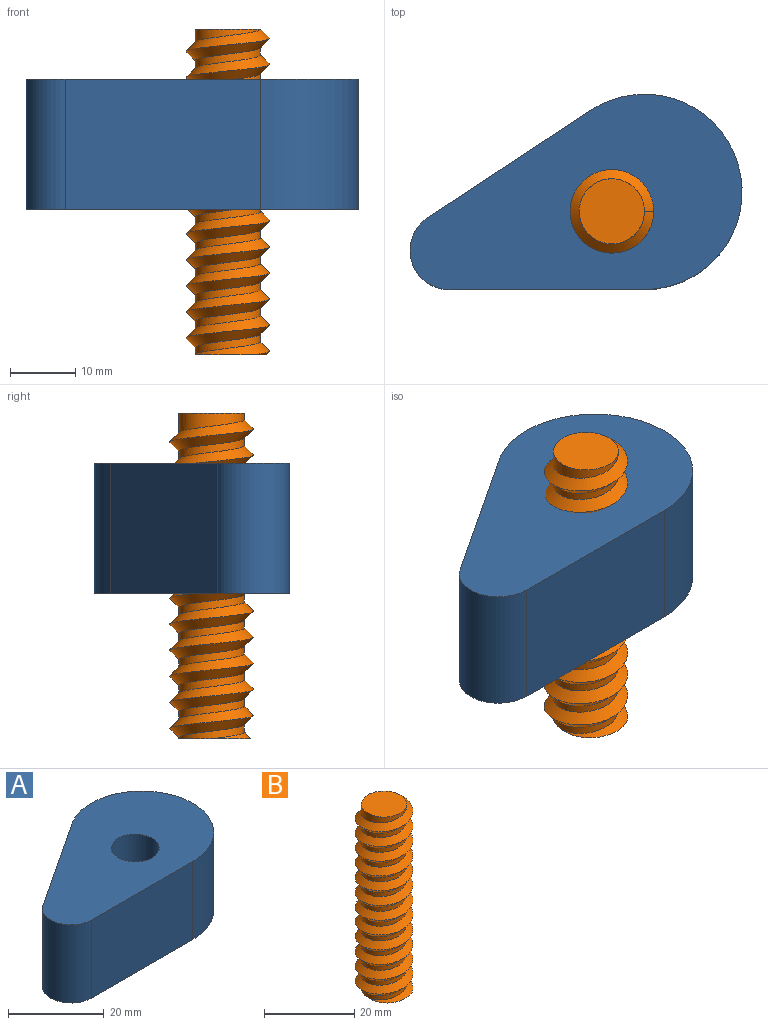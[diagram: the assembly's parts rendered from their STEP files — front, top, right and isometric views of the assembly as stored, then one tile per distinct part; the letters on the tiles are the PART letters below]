
ASSEMBLY  parts=2 mates=1
PART A: 7 faces, bbox 51x30x20 mm
  f0: plane 25.05x20mm, normal (-0.55,0.83,0), area 600mm2, adj f1,f3,f4,f5
  f1: cylinder r=6mm len=20mm, axis (0,0,-1), area 307mm2, adj f0,f2,f4,f5
  f2: plane 30x20mm, normal (0,-1,0), area 600mm2, adj f1,f3,f4,f5
  f3: cylinder r=15mm len=30mm, axis (0,0,-1), area 1117.4mm2, adj f0,f2,f4,f5
  f4: plane 51x30mm, normal (0,0,1), area 1016.5mm2, adj f0,f1,f2,f3,f6
  f5: plane 51x30mm, normal (0,0,-1), area 1016.5mm2, adj f0,f1,f2,f3,f6
  f6: cylinder r=5mm len=20mm, axis (0,0,1), area 628.3mm2, adj f4,f5
PART B: 6 faces, bbox 13.7x15.6x52.3 mm
  f0: cylinder r=5mm len=50mm, axis (0,0,-1), area 529.9mm2, adj f1,f2,f3,f4,f5
  f1: plane 10x10mm, normal (0,0,1), area 78.5mm2, adj f0
  f2: plane 11.87x11.72mm, normal (0,0,-1), area 95.7mm2, adj f0,f4,f5
  f3: plane 2.83x1.41mm, normal (0,1,0), area 2mm2, adj f0,f4,f5
  f4: bspline ~51.41x14.81mm, area 888mm2, adj f0,f2,f3,f5
  f5: bspline ~50.08x14.81mm, area 863.1mm2, adj f0,f2,f3,f4
PLACE A t=(-19.74,-2.75,-8.74)mm
PLACE B t=(25.26,9.25,-31.09)mm
MATE slider B.f0 <-> A.f6  axis (0,0,-1) through (25.26,9.25,18.91)mm
